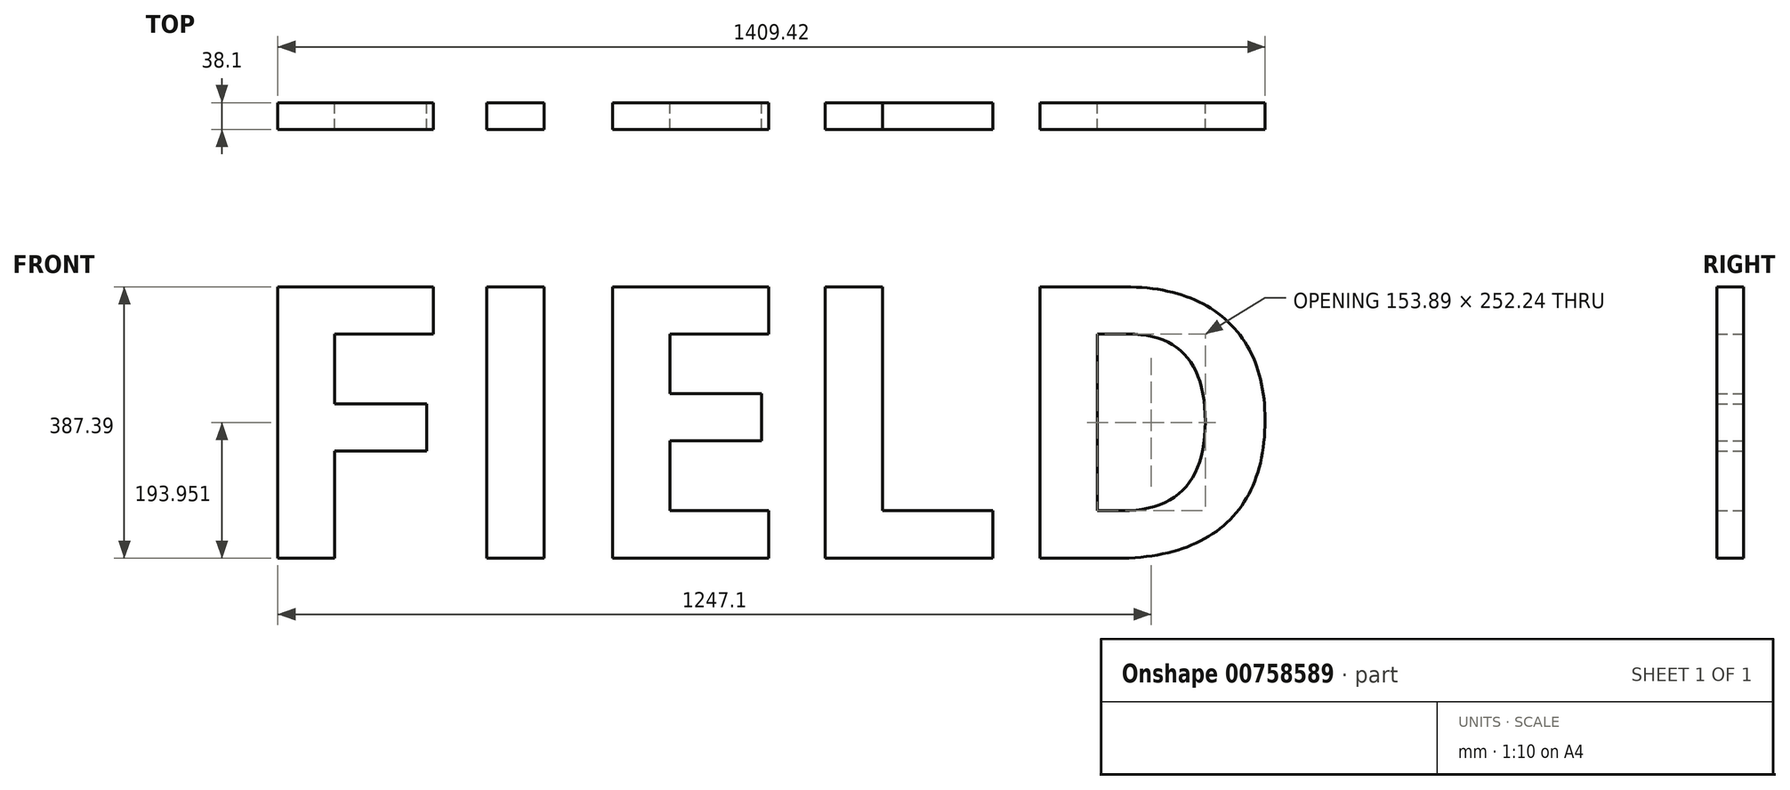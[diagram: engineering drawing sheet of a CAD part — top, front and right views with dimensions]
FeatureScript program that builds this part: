
annotation { "Feature Type Name" : "Feature", "Feature Type Description" : "" }
export const myFeature = defineFeature(function(context is Context, id is Id, definition is map)
    precondition{}
    {
        {
            var Q0;
            Q0=qCreatedBy(makeId("Front.planeOp"),FACE);
            var sketch = newSketch(context, id + "F0", { "sketchPlane" : qUnion([Q0])});
            skLineSegment(sketch, "E0.bottom", {"start": v(-762, 228.6) * mm, "end": v(762, 228.6) * mm});
            skLineSegment(sketch, "E0.top", {"start": v(-762, -228.6) * mm, "end": v(762, -228.6) * mm});
            skLineSegment(sketch, "E0.left", {"start": v(-762, 228.6) * mm, "end": v(-762, -228.6) * mm});
            skLineSegment(sketch, "E0.right", {"start": v(762, 228.6) * mm, "end": v(762, -228.6) * mm});
            skPoint(sketch, "E0.middle", {"position": v(0, 0) * mm});
            skText(sketch, "E1", { "text": "FIELD", "fontName": "OpenSans-Bold.ttf"});
            const initialGuessF0  = {"E1": [-0.74255, -0.19243, 1, 0, 0.3907]};
            skSetInitialGuess(sketch, initialGuessF0);
            skSolve(sketch);
        }
        {
            var Q0;
            Q0=makeQuery(id+"F0.imprint","IMPRINT",FACE,{"disambiguationData":[TD([[makeQuery(id+"F0.imprint","IMPRINT",EDGE,{"derivedFrom":sQuery(id+"F0.wireOp",EDGE,"E1.sketch_text.stroke-0")}),-1.0]])]});
            var Q1;
            Q1=makeQuery(id+"F0.imprint","IMPRINT",FACE,{"disambiguationData":[TD([[makeQuery(id+"F0.imprint","IMPRINT",EDGE,{"derivedFrom":sQuery(id+"F0.wireOp",EDGE,"E1.sketch_text.stroke-10")}),-1.0]])]});
            var Q2;
            Q2=makeQuery(id+"F0.imprint","IMPRINT",FACE,{"disambiguationData":[TD([[makeQuery(id+"F0.imprint","IMPRINT",EDGE,{"derivedFrom":sQuery(id+"F0.wireOp",EDGE,"E1.sketch_text.stroke-14")}),-1.0]])]});
            var Q3;
            Q3=makeQuery(id+"F0.imprint","IMPRINT",FACE,{"disambiguationData":[TD([[makeQuery(id+"F0.imprint","IMPRINT",EDGE,{"derivedFrom":sQuery(id+"F0.wireOp",EDGE,"E1.sketch_text.stroke-26")}),-1.0]])]});
            var Q4;
            Q4=makeQuery(id+"F0.imprint","IMPRINT",FACE,{"disambiguationData":[TD([[makeQuery(id+"F0.imprint","IMPRINT",EDGE,{"derivedFrom":sQuery(id+"F0.wireOp",EDGE,"E1.sketch_text.stroke-32")}),-1.0]])]});
            extrude(context, id + "F1", {"entities" : qUnion([Q0, Q1, Q2, Q3, Q4]), "depth" : 38.1 * mm, "offsetDistance" : 25.4 * mm});
        }
    });
